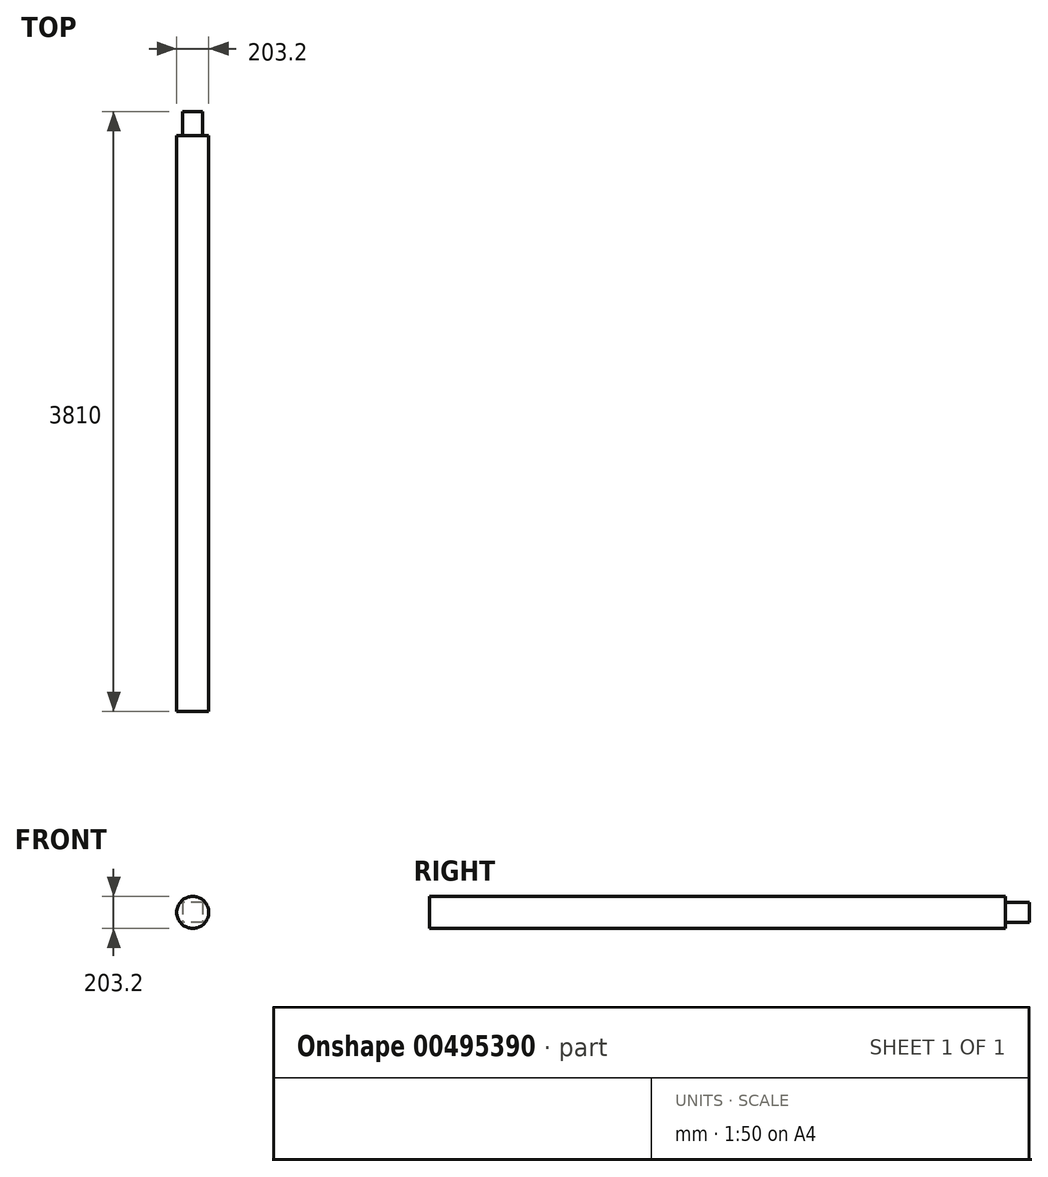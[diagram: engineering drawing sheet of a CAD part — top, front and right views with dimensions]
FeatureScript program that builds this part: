
annotation { "Feature Type Name" : "Feature", "Feature Type Description" : "" }
export const myFeature = defineFeature(function(context is Context, id is Id, definition is map)
    precondition{}
    {
        {
            var Q0;
            Q0=qCreatedBy(makeId("Front.planeOp"),FACE);
            var sketch = newSketch(context, id + "F0", { "sketchPlane" : qUnion([Q0])});
            skCircle(sketch, "E0", {"center": v(0, 0) * mm, "radius": 101.6 * mm});
            skSolve(sketch);
        }
        {
            var Q0;
            Q0 = qSketchRegion(id + "F0", true);
            extrude(context, id + "F1", {"entities" : qUnion([Q0]), "depth" : 3657.6 * mm, "offsetDistance" : 25.4 * mm});
        }
        {
            var Q0;
            Q0=makeQuery(id+"F1.opExtrude","CAP_FACE",FACE,{"disambiguationData":[OSD([sQuery(id+"F0.wireOp",EDGE,"E0")])],"isStart":true});
            var sketch = newSketch(context, id + "F2", { "sketchPlane" : qUnion([Q0])});
            skLineSegment(sketch, "E1.bottom", {"start": v(-63.5, 63.5) * mm, "end": v(63.5, 63.5) * mm});
            skLineSegment(sketch, "E1.top", {"start": v(-63.5, -63.5) * mm, "end": v(63.5, -63.5) * mm});
            skLineSegment(sketch, "E1.left", {"start": v(-63.5, 63.5) * mm, "end": v(-63.5, -63.5) * mm});
            skLineSegment(sketch, "E1.right", {"start": v(63.5, 63.5) * mm, "end": v(63.5, -63.5) * mm});
            skSolve(sketch);
        }
        {
            var Q0;
            Q0 = qSketchRegion(id + "F2", true);
            extrude(context, id + "F3", {"entities" : qUnion([Q0]), "operationType" : NewBodyOperationType.ADD, "depth" : 152.4 * mm, "offsetDistance" : 25.4 * mm});
        }
    });
